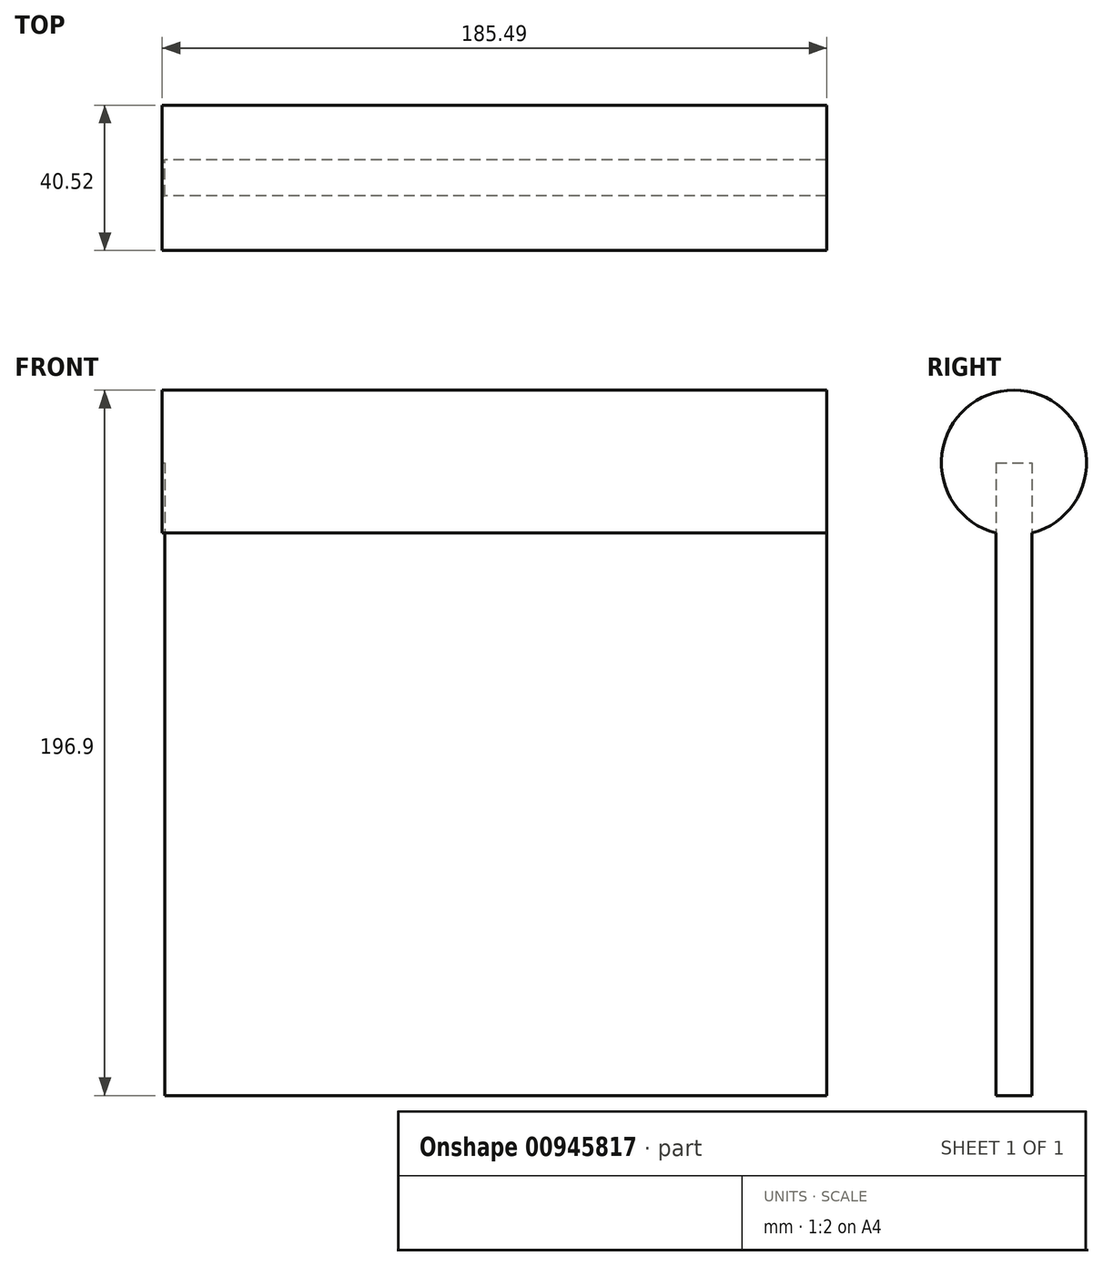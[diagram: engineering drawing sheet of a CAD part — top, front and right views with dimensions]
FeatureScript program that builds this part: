
annotation { "Feature Type Name" : "Feature", "Feature Type Description" : "" }
export const myFeature = defineFeature(function(context is Context, id is Id, definition is map)
    precondition{}
    {
        {
            var Q0;
            Q0=qCreatedBy(makeId("Front.planeOp"),FACE);
            var sketch = newSketch(context, id + "F0", { "sketchPlane" : qUnion([Q0])});
            skLineSegment(sketch, "E0.bottom", {"start": v(92.39, 88.32) * mm, "end": v(-92.39, 88.32) * mm});
            skLineSegment(sketch, "E0.top", {"start": v(92.39, -88.32) * mm, "end": v(-92.39, -88.32) * mm});
            skLineSegment(sketch, "E0.left", {"start": v(92.39, 88.32) * mm, "end": v(92.39, -88.32) * mm});
            skLineSegment(sketch, "E0.right", {"start": v(-92.39, 88.32) * mm, "end": v(-92.39, -88.32) * mm});
            skPoint(sketch, "E0.middle", {"position": v(0, 0) * mm});
            skSolve(sketch);
        }
        {
            var Q0;
            Q0=makeQuery(id+"F0.imprint","IMPRINT",FACE,{"disambiguationData":[TD([[makeQuery(id+"F0.imprint","IMPRINT",EDGE,{"derivedFrom":sQuery(id+"F0.wireOp",EDGE,"E0.bottom")}),1.0]])]});
            extrude(context, id + "F1", {"entities" : qUnion([Q0]), "depth" : 10 * mm, "offsetDistance" : 25.4 * mm});
        }
        {
            var Q0;
            Q0=makeQuery(id+"F1.opExtrude","SWEPT_FACE",FACE,{"disambiguationData":[OSD([sQuery(id+"F0.wireOp",EDGE,"E0.left")])]});
            var sketch = newSketch(context, id + "F2", { "sketchPlane" : qUnion([Q0])});
            skCircle(sketch, "E1", {"center": v(-5, 88.32) * mm, "radius": 20.26 * mm});
            skSolve(sketch);
        }
        {
            var Q0;
            {var subQ1=sQuery(id+"F0.wireOp",EDGE,"E0.left");var subQ6=makeQuery(id+"F1.opExtrude","SWEPT_EDGE",EDGE,{"disambiguationData":[OSD([sQuery(id+"F0.wireOp",EDGE,"E0.bottom"),subQ1])]});Q0=makeQuery(id+"F2.imprint","IMPRINT",FACE,{"disambiguationData":[TD([[makeQuery(id+"F2.imprint","IMPRINT",EDGE,{"derivedFrom":subQ6}),1.0]])]});}
            extrude(context, id + "F3", {"entities" : qUnion([Q0]), "operationType" : NewBodyOperationType.ADD, "oppositeDirection" : true, "depth" : 185.5 * mm, "offsetDistance" : 25.4 * mm});
        }
    });
